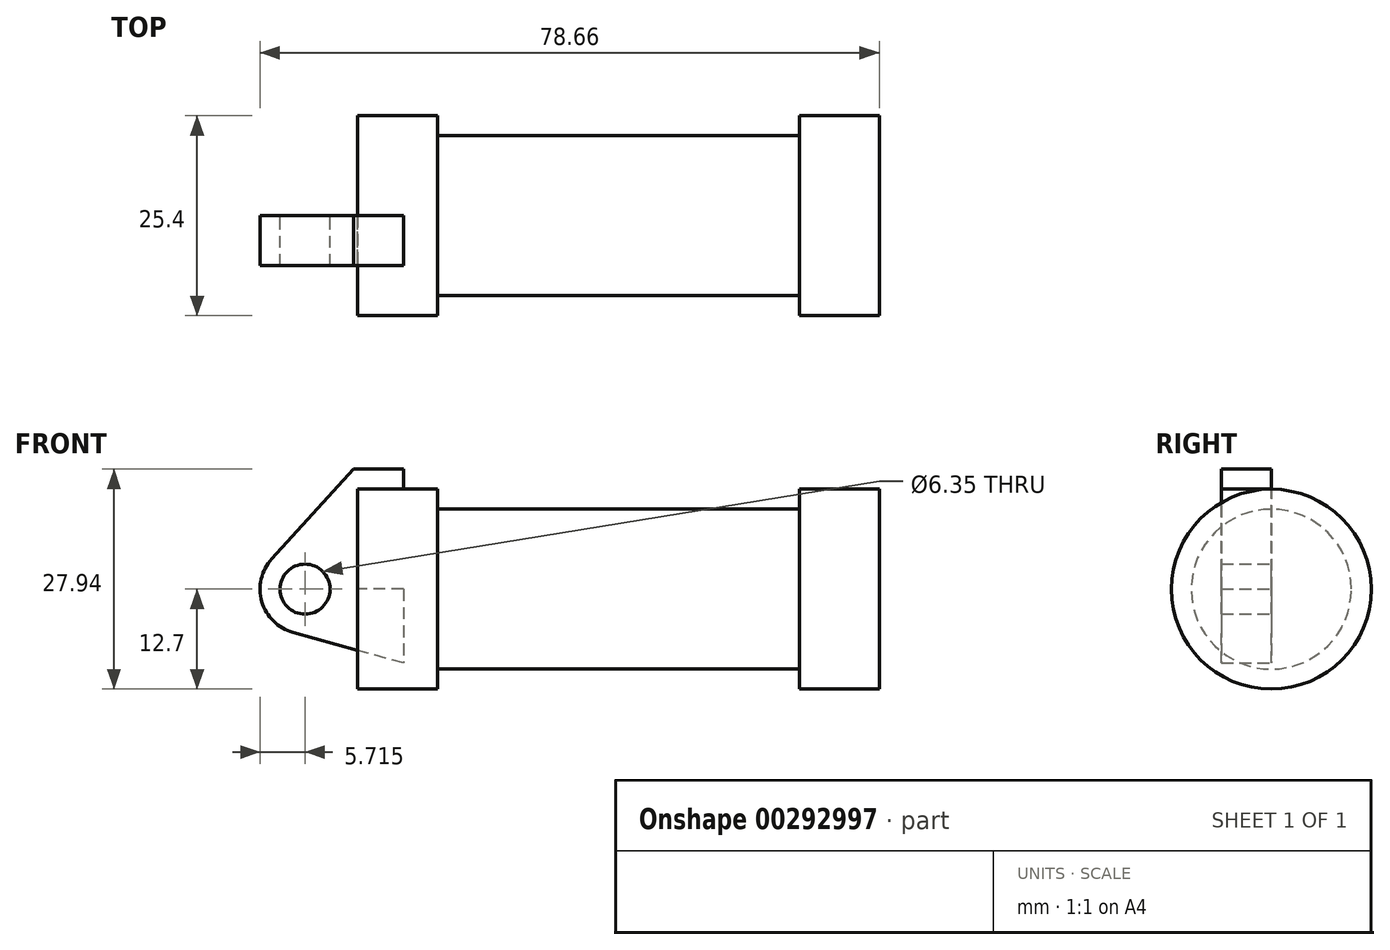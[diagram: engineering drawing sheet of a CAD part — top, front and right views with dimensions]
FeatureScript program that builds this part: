
annotation { "Feature Type Name" : "Feature", "Feature Type Description" : "" }
export const myFeature = defineFeature(function(context is Context, id is Id, definition is map)
    precondition{}
    {
        {
            var Q0;
            Q0=qCreatedBy(makeId("Front.planeOp"),FACE);
            var sketch = newSketch(context, id + "F0", { "sketchPlane" : qUnion([Q0])});
            skLineSegment(sketch, "E0", {"start": v(0, 0) * mm, "end": v(0, 12.7) * mm});
            skLineSegment(sketch, "E1", {"start": v(0, 12.7) * mm, "end": v(10.16, 12.7) * mm});
            skLineSegment(sketch, "E2", {"start": v(10.16, 12.7) * mm, "end": v(10.16, 10.16) * mm});
            skLineSegment(sketch, "E3", {"start": v(10.16, 10.16) * mm, "end": v(56.13, 10.16) * mm});
            skLineSegment(sketch, "E4", {"start": v(56.13, 10.16) * mm, "end": v(56.13, 12.7) * mm});
            skLineSegment(sketch, "E5", {"start": v(56.13, 12.7) * mm, "end": v(66.3, 12.7) * mm});
            skLineSegment(sketch, "E6", {"start": v(66.3, 12.7) * mm, "end": v(66.3, 0) * mm});
            skLineSegment(sketch, "E7", {"start": v(66.3, 0) * mm, "end": v(0, 0) * mm});
            skLineSegment(sketch, "E8", {"start": v(5.84, 15.24) * mm, "end": v(-0.5, 15.24) * mm});
            skLineSegment(sketch, "E9", {"start": v(-0.5, 15.24) * mm, "end": v(-10.88, 3.85) * mm});
            skLineSegment(sketch, "E10", {"start": v(0, 0) * mm, "end": v(-6.65, 0) * mm});
            skCircle(sketch, "E11", {"center": v(-6.65, 0) * mm, "radius": 5.72 * mm});
            skCircle(sketch, "E12", {"center": v(-6.65, 0) * mm, "radius": 3.18 * mm});
            skLineSegment(sketch, "E13", {"start": v(5.84, 15.24) * mm, "end": v(5.84, -9.4) * mm});
            skLineSegment(sketch, "E14", {"start": v(5.84, -9.4) * mm, "end": v(-8.18, -5.5) * mm});
            skSolve(sketch);
        }
        {
            var Q0;
            {var subQ0=sQuery(id+"F0.wireOp",EDGE,"E2");Q0=makeQuery(id+"F0.imprint","IMPRINT",FACE,{"disambiguationData":[TD([[makeQuery(id+"F0.imprint","IMPRINT",EDGE,{"derivedFrom":subQ0}),-1.0]])]});}
            var Q1;
            {var subQ0=sQuery(id+"F0.wireOp",EDGE,"E0");Q1=makeQuery(id+"F0.imprint","IMPRINT",FACE,{"disambiguationData":[TD([[makeQuery(id+"F0.imprint","IMPRINT",EDGE,{"derivedFrom":subQ0}),-1.0]])]});}
            var Q2;
            Q2=sQuery(id+"F0.wireOp",EDGE,"E7");
            revolve(context, id + "F1", {"entities" : qUnion([Q0, Q1]), "axis" : qUnion([Q2]), "revolveType" : RevolveType.FULL});
        }
        {
            var Q0;
            {var subQ1=sQuery(id+"F0.wireOp",EDGE,"E0");Q0=makeQuery(id+"F0.imprint","IMPRINT",FACE,{"disambiguationData":[TD([[makeQuery(id+"F0.imprint","IMPRINT",EDGE,{"derivedFrom":subQ1}),1.0]])]});}
            var Q1;
            {var subQ5=sQuery(id+"F0.wireOp",EDGE,"E12");Q1=makeQuery(id+"F0.imprint","IMPRINT",FACE,{"disambiguationData":[TD([[makeQuery(id+"F0.imprint","IMPRINT",EDGE,{"derivedFrom":subQ5}),-1.0]])]});}
            var Q2;
            {var subQ0=sQuery(id+"F0.wireOp",EDGE,"E14");Q2=makeQuery(id+"F0.imprint","IMPRINT",FACE,{"disambiguationData":[TD([[makeQuery(id+"F0.imprint","IMPRINT",EDGE,{"derivedFrom":subQ0}),-1.0]])]});}
            extrude(context, id + "F2", {"entities" : qUnion([Q0, Q1, Q2]), "depth" : 6.35 * mm});
        }
    });
